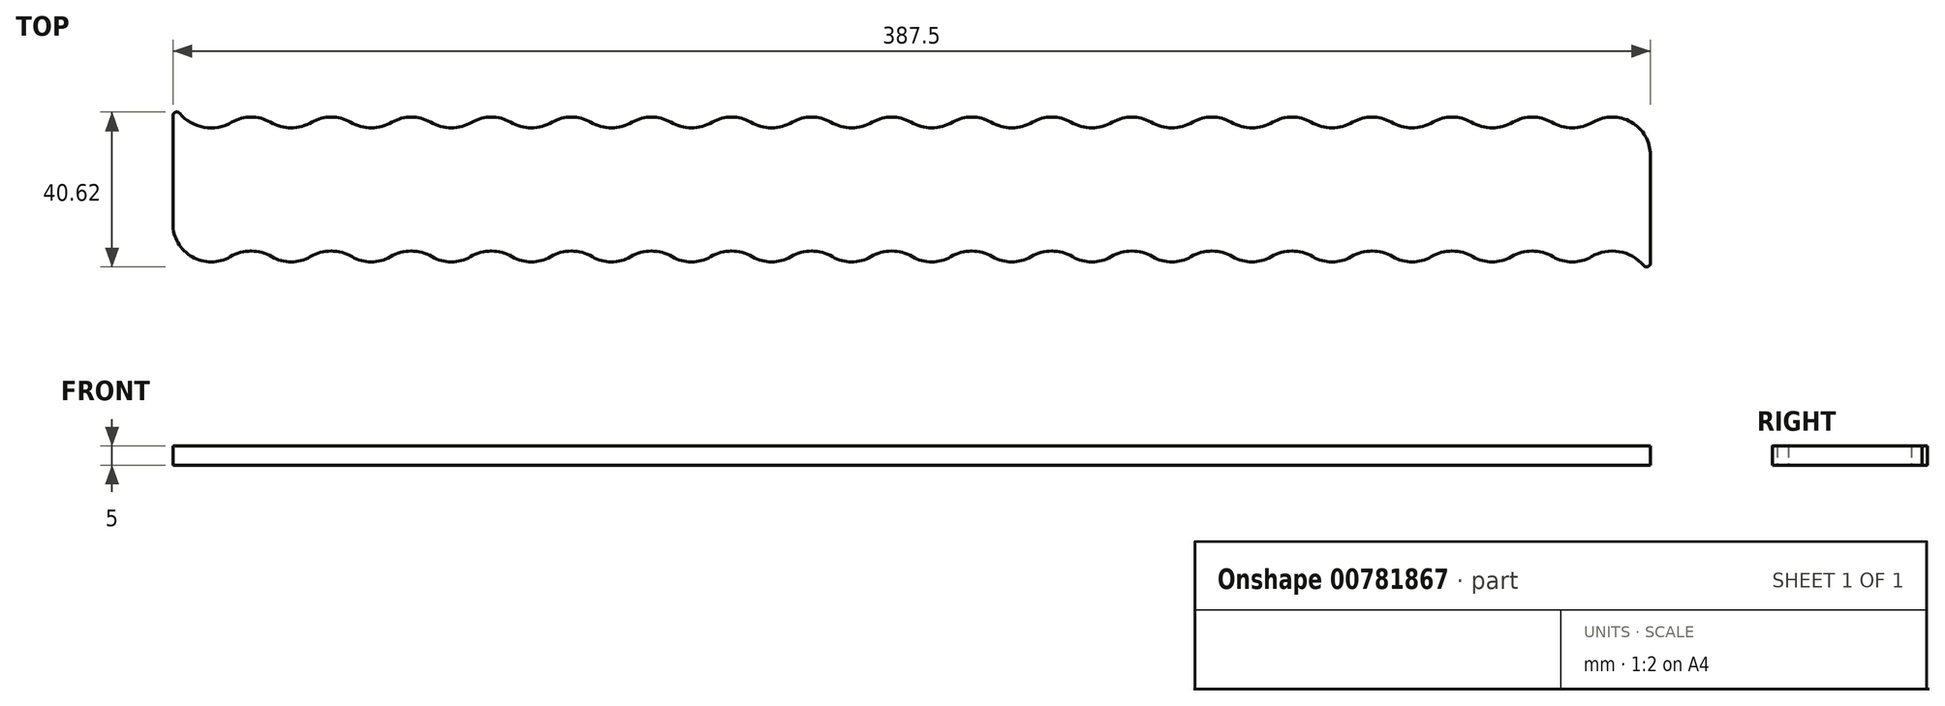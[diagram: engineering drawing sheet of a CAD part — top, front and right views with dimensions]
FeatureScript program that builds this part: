
annotation { "Feature Type Name" : "Feature", "Feature Type Description" : "" }
export const myFeature = defineFeature(function(context is Context, id is Id, definition is map)
    precondition{}
    {
        {
            var Q0;
            Q0=qCreatedBy(makeId("Top.planeOp"),FACE);
            var sketch = newSketch(context, id + "F0", { "sketchPlane" : qUnion([Q0])});
            skCircle(sketch, "E0", {"center": v(-87, 0) * mm, "radius": 10 * mm});
            skCircle(sketch, "E1.1.0.0", {"center": v(-66, 0) * mm, "radius": 10 * mm});
            skCircle(sketch, "E1.2.0.0", {"center": v(-45, 0) * mm, "radius": 10 * mm});
            skCircle(sketch, "E1.3.0.0", {"center": v(-24, 0) * mm, "radius": 10 * mm});
            skCircle(sketch, "E1.4.0.0", {"center": v(-3, 0) * mm, "radius": 10 * mm});
            skLineSegment(sketch, "E1.direction1", {"start": v(-87, 0) * mm, "end": v(-66, 0) * mm, "construction": true});
            skLineSegment(sketch, "E2", {"start": v(-76.5, 0) * mm, "end": v(-76.5, -18) * mm, "construction": true});
            skArc(sketch, "E3", {"start": v(-71.05, -8.64) * mm, "mid": v(-76.5, -7.16) * mm, "end": v(-81.97, -8.64) * mm});
            skArc(sketch, "E4.1.0.0", {"start": v(-50.05, -8.64) * mm, "mid": v(-55.5, -7.16) * mm, "end": v(-60.97, -8.64) * mm});
            skArc(sketch, "E4.2.0.0", {"start": v(-29.05, -8.64) * mm, "mid": v(-34.5, -7.16) * mm, "end": v(-39.97, -8.64) * mm});
            skArc(sketch, "E4.3.0.0", {"start": v(-8.05, -8.64) * mm, "mid": v(-13.5, -7.16) * mm, "end": v(-18.97, -8.64) * mm});
            skLineSegment(sketch, "E4.direction1", {"start": v(-76.5, -18) * mm, "end": v(-55.5, -18) * mm, "construction": true});
            skLineSegment(sketch, "E5", {"start": v(-76.5, 0) * mm, "end": v(-76.5, 18) * mm, "construction": true});
            skCircle(sketch, "E6", {"center": v(-76.5, 18) * mm, "radius": 10 * mm});
            skCircle(sketch, "E7.1.0.0", {"center": v(-55.5, 18) * mm, "radius": 10 * mm});
            skCircle(sketch, "E7.2.0.0", {"center": v(-34.5, 18) * mm, "radius": 10 * mm});
            skCircle(sketch, "E7.3.0.0", {"center": v(-13.5, 18) * mm, "radius": 10 * mm});
            skCircle(sketch, "E7.4.0.0", {"center": v(7.5, 18) * mm, "radius": 10 * mm});
            skLineSegment(sketch, "E7.direction1", {"start": v(-76.5, 18) * mm, "end": v(-55.5, 18) * mm, "construction": true});
            skLineSegment(sketch, "E8", {"start": v(-66, 18) * mm, "end": v(-66, 36) * mm, "construction": true});
            skArc(sketch, "E9", {"start": v(-71.47, 26.64) * mm, "mid": v(-66, 25.16) * mm, "end": v(-60.55, 26.64) * mm});
            skLineSegment(sketch, "E10.direction1", {"start": v(-71.47, 26.64) * mm, "end": v(-50.47, 26.64) * mm, "construction": true});
            skLineSegment(sketch, "E11", {"start": v(-97, 0) * mm, "end": v(-97, 31.82) * mm});
            skArc(sketch, "E12.1.0.0", {"start": v(-97, 31.82) * mm, "mid": v(-90.45, 25.72) * mm, "end": v(-81.55, 26.64) * mm});
            skLineSegment(sketch, "E12.direction1", {"start": v(-71.47, 26.64) * mm, "end": v(-92.47, 26.64) * mm, "construction": true});
            skPoint(sketch, "E13.start.orphan", {"position": v(-76.5, 28) * mm});
            skArc(sketch, "E14.1.0.0", {"start": v(12.95, -8.64) * mm, "mid": v(7.5, -7.16) * mm, "end": v(2.03, -8.64) * mm});
            skLineSegment(sketch, "E14.direction1", {"start": v(-13.5, -18) * mm, "end": v(7.5, -18) * mm, "construction": true});
            skPoint(sketch, "E15.start.orphan", {"position": v(-3, -10) * mm});
            skPoint(sketch, "E16.orphan", {"position": v(12.95, -8.64) * mm});
            skCircle(sketch, "E17.0.5.0", {"center": v(18, 0) * mm, "radius": 10 * mm});
            skCircle(sketch, "E17.0.6.0", {"center": v(39, 0) * mm, "radius": 10 * mm});
            skCircle(sketch, "E17.0.7.0", {"center": v(60, 0) * mm, "radius": 10 * mm});
            skCircle(sketch, "E17.0.8.0", {"center": v(81, 0) * mm, "radius": 10 * mm});
            skCircle(sketch, "E17.0.9.0", {"center": v(102, 0) * mm, "radius": 10 * mm});
            skCircle(sketch, "E17.0.10.0", {"center": v(123, 0) * mm, "radius": 10 * mm});
            skCircle(sketch, "E17.0.11.0", {"center": v(144, 0) * mm, "radius": 10 * mm});
            skCircle(sketch, "E17.0.12.0", {"center": v(165, 0) * mm, "radius": 10 * mm});
            skCircle(sketch, "E17.0.13.0", {"center": v(186, 0) * mm, "radius": 10 * mm});
            skCircle(sketch, "E17.0.14.0", {"center": v(207, 0) * mm, "radius": 10 * mm});
            skCircle(sketch, "E17.0.15.0", {"center": v(228, 0) * mm, "radius": 10 * mm});
            skCircle(sketch, "E17.0.16.0", {"center": v(249, 0) * mm, "radius": 10 * mm});
            skCircle(sketch, "E17.0.17.0", {"center": v(270, 0) * mm, "radius": 10 * mm});
            skCircle(sketch, "E18.0.5.0", {"center": v(28.5, 18) * mm, "radius": 10 * mm});
            skCircle(sketch, "E18.0.6.0", {"center": v(49.5, 18) * mm, "radius": 10 * mm});
            skCircle(sketch, "E18.0.7.0", {"center": v(70.5, 18) * mm, "radius": 10 * mm});
            skCircle(sketch, "E18.0.8.0", {"center": v(91.5, 18) * mm, "radius": 10 * mm});
            skCircle(sketch, "E18.0.9.0", {"center": v(112.5, 18) * mm, "radius": 10 * mm});
            skCircle(sketch, "E18.0.10.0", {"center": v(133.5, 18) * mm, "radius": 10 * mm});
            skCircle(sketch, "E18.0.11.0", {"center": v(154.5, 18) * mm, "radius": 10 * mm});
            skCircle(sketch, "E18.0.12.0", {"center": v(175.5, 18) * mm, "radius": 10 * mm});
            skCircle(sketch, "E18.0.13.0", {"center": v(196.5, 18) * mm, "radius": 10 * mm});
            skCircle(sketch, "E18.0.14.0", {"center": v(217.5, 18) * mm, "radius": 10 * mm});
            skCircle(sketch, "E18.0.15.0", {"center": v(238.5, 18) * mm, "radius": 10 * mm});
            skCircle(sketch, "E18.0.16.0", {"center": v(259.5, 18) * mm, "radius": 10 * mm});
            skCircle(sketch, "E18.0.17.0", {"center": v(280.5, 18) * mm, "radius": 10 * mm});
            skArc(sketch, "E19.0.1.0", {"start": v(-50.47, 26.64) * mm, "mid": v(-45, 25.16) * mm, "end": v(-39.55, 26.64) * mm});
            skArc(sketch, "E19.0.2.0", {"start": v(-29.47, 26.64) * mm, "mid": v(-24, 25.16) * mm, "end": v(-18.55, 26.64) * mm});
            skArc(sketch, "E19.0.3.0", {"start": v(-8.47, 26.64) * mm, "mid": v(-3, 25.16) * mm, "end": v(2.45, 26.64) * mm});
            skArc(sketch, "E19.0.4.0", {"start": v(12.53, 26.64) * mm, "mid": v(18, 25.16) * mm, "end": v(23.45, 26.64) * mm});
            skArc(sketch, "E19.0.5.0", {"start": v(33.53, 26.64) * mm, "mid": v(39, 25.16) * mm, "end": v(44.45, 26.64) * mm});
            skArc(sketch, "E19.0.6.0", {"start": v(54.53, 26.64) * mm, "mid": v(60, 25.16) * mm, "end": v(65.45, 26.64) * mm});
            skArc(sketch, "E19.0.7.0", {"start": v(75.53, 26.64) * mm, "mid": v(81, 25.16) * mm, "end": v(86.45, 26.64) * mm});
            skArc(sketch, "E19.0.8.0", {"start": v(96.53, 26.64) * mm, "mid": v(102, 25.16) * mm, "end": v(107.45, 26.64) * mm});
            skArc(sketch, "E19.0.9.0", {"start": v(117.53, 26.64) * mm, "mid": v(123, 25.16) * mm, "end": v(128.45, 26.64) * mm});
            skArc(sketch, "E19.0.10.0", {"start": v(138.53, 26.64) * mm, "mid": v(144, 25.16) * mm, "end": v(149.45, 26.64) * mm});
            skArc(sketch, "E19.0.11.0", {"start": v(159.53, 26.64) * mm, "mid": v(165, 25.16) * mm, "end": v(170.45, 26.64) * mm});
            skArc(sketch, "E19.0.12.0", {"start": v(180.53, 26.64) * mm, "mid": v(186, 25.16) * mm, "end": v(191.45, 26.64) * mm});
            skArc(sketch, "E19.0.13.0", {"start": v(201.53, 26.64) * mm, "mid": v(207, 25.16) * mm, "end": v(212.45, 26.64) * mm});
            skArc(sketch, "E19.0.14.0", {"start": v(222.53, 26.64) * mm, "mid": v(228, 25.16) * mm, "end": v(233.45, 26.64) * mm});
            skArc(sketch, "E19.0.15.0", {"start": v(243.53, 26.64) * mm, "mid": v(249, 25.16) * mm, "end": v(254.45, 26.64) * mm});
            skArc(sketch, "E19.0.16.0", {"start": v(264.53, 26.64) * mm, "mid": v(270, 25.16) * mm, "end": v(275.45, 26.64) * mm});
            skArc(sketch, "E20.0.5.0", {"start": v(33.95, -8.64) * mm, "mid": v(28.5, -7.16) * mm, "end": v(23.03, -8.64) * mm});
            skArc(sketch, "E20.0.6.0", {"start": v(54.95, -8.64) * mm, "mid": v(49.5, -7.16) * mm, "end": v(44.03, -8.64) * mm});
            skArc(sketch, "E20.0.7.0", {"start": v(75.95, -8.64) * mm, "mid": v(70.5, -7.16) * mm, "end": v(65.03, -8.64) * mm});
            skArc(sketch, "E20.0.8.0", {"start": v(96.95, -8.64) * mm, "mid": v(91.5, -7.16) * mm, "end": v(86.03, -8.64) * mm});
            skArc(sketch, "E20.0.9.0", {"start": v(117.95, -8.64) * mm, "mid": v(112.5, -7.16) * mm, "end": v(107.03, -8.64) * mm});
            skArc(sketch, "E20.0.10.0", {"start": v(138.95, -8.64) * mm, "mid": v(133.5, -7.16) * mm, "end": v(128.03, -8.64) * mm});
            skArc(sketch, "E20.0.11.0", {"start": v(159.95, -8.64) * mm, "mid": v(154.5, -7.16) * mm, "end": v(149.03, -8.64) * mm});
            skArc(sketch, "E20.0.12.0", {"start": v(180.95, -8.64) * mm, "mid": v(175.5, -7.16) * mm, "end": v(170.03, -8.64) * mm});
            skArc(sketch, "E20.0.13.0", {"start": v(201.95, -8.64) * mm, "mid": v(196.5, -7.16) * mm, "end": v(191.03, -8.64) * mm});
            skArc(sketch, "E20.0.14.0", {"start": v(222.95, -8.64) * mm, "mid": v(217.5, -7.16) * mm, "end": v(212.03, -8.64) * mm});
            skArc(sketch, "E20.0.15.0", {"start": v(243.95, -8.64) * mm, "mid": v(238.5, -7.16) * mm, "end": v(233.03, -8.64) * mm});
            skArc(sketch, "E20.0.16.0", {"start": v(264.95, -8.64) * mm, "mid": v(259.5, -7.16) * mm, "end": v(254.03, -8.64) * mm});
            skArc(sketch, "E21.0.17.0", {"start": v(290.5, -13.82) * mm, "mid": v(283.94, -7.72) * mm, "end": v(275.03, -8.64) * mm});
            skLineSegment(sketch, "E22", {"start": v(290.5, 18) * mm, "end": v(290.5, -13.82) * mm});
            skPoint(sketch, "E23.orphan", {"position": v(285.95, -8.64) * mm});
            skSolve(sketch);
        }
        {
            var Q0;
            Q0 = qSketchRegion(id + "F0", true);
            extrude(context, id + "F1", {"entities" : qUnion([Q0]), "depth" : 5 * mm, "offsetDistance" : 25 * mm});
        }
        {
            var Q0;
            Q0=makeQuery(id+"F1.opExtrude","SWEPT_EDGE",EDGE,{"disambiguationData":[OSD([sQuery(id+"F0.wireOp",EDGE,"E21.0.17.0"),sQuery(id+"F0.wireOp",EDGE,"E22")])]});
            var Q1;
            Q1=makeQuery(id+"F1.opExtrude","SWEPT_EDGE",EDGE,{"disambiguationData":[OSD([sQuery(id+"F0.wireOp",EDGE,"E11"),sQuery(id+"F0.wireOp",EDGE,"E12.1.0.0")])]});
            fillet(context, id + "F2", {"entities" : qUnion([Q0, Q1]), "radius" : 1 * mm, "tangentPropagation" : true, "allowEdgeOverflow" : false});
        }
    });
